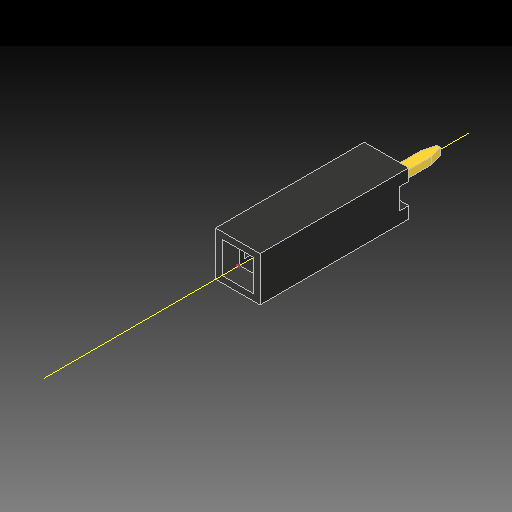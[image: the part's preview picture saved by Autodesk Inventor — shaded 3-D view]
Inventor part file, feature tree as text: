
AUTODESK INVENTOR PART (.ipt)
format: ipt  version: 2020 (Build 240168000, 168)  size: 141,312 bytes
history: native  units: mm
features: sketch x1, other x1, imported_body x1
ambient origin geometry x8: Origin, YZ Plane, XZ Plane, XY Plane, X Axis, Y Axis, Z Axis, Center Point
bodies: Solid1 (feature_tree)
feature tree (3):
  sketch  "Sketch1"
  other  "Work Axis1"
  imported_body  "Base1"
